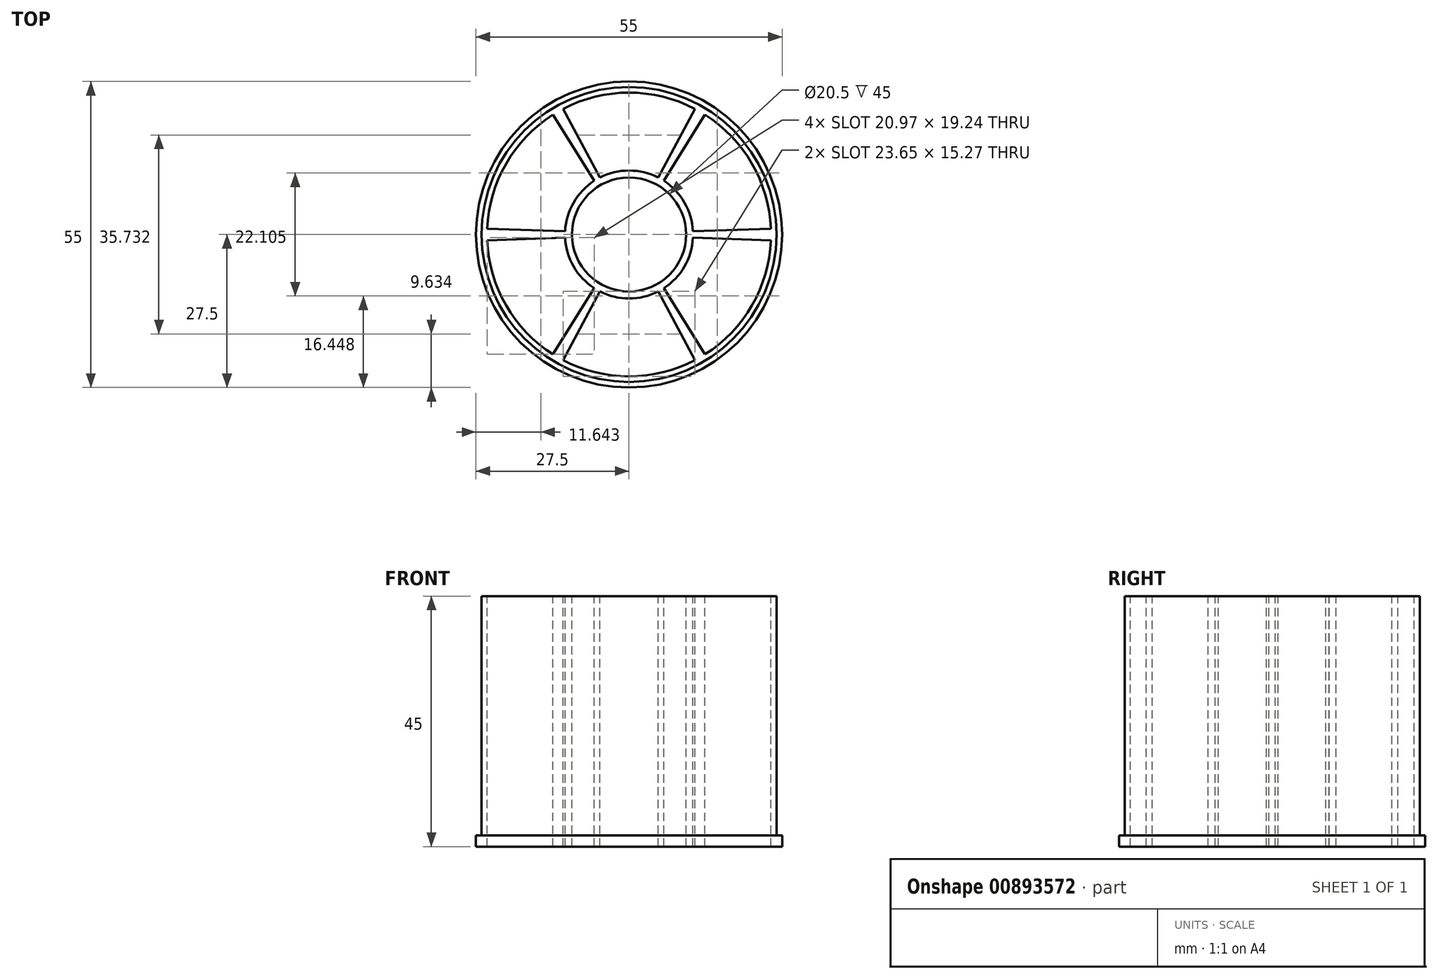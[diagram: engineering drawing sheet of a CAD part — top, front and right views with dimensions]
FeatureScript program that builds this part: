
annotation { "Feature Type Name" : "Feature", "Feature Type Description" : "" }
export const myFeature = defineFeature(function(context is Context, id is Id, definition is map)
    precondition{}
    {
        {
            var Q0;
            Q0=qCreatedBy(makeId("Top.planeOp"),FACE);
            var sketch = newSketch(context, id + "F0", { "sketchPlane" : qUnion([Q0])});
            skCircle(sketch, "E0", {"center": v(0, 0) * mm, "radius": 27.5 * mm});
            skSolve(sketch);
        }
        {
            var Q0;
            Q0 = qSketchRegion(id + "F0", true);
            extrude(context, id + "F1", {"entities" : qUnion([Q0]), "depth" : 45 * mm, "offsetDistance" : 25 * mm});
        }
        {
            var Q0;
            Q0=makeQuery(id+"F1.opExtrude","CAP_FACE",FACE,{"disambiguationData":[OSD([sQuery(id+"F0.wireOp",EDGE,"E0")])],"isStart":false});
            var sketch = newSketch(context, id + "F2", { "sketchPlane" : qUnion([Q0])});
            skCircle(sketch, "E1", {"center": v(0, 0) * mm, "radius": 26.5 * mm});
            skCircle(sketch, "E2", {"center": v(0, 0) * mm, "radius": 41.57 * mm});
            skSolve(sketch);
        }
        {
            var Q0;
            Q0 = qSketchRegion(id + "F2", true);
            extrude(context, id + "F3", {"entities" : qUnion([Q0]), "operationType" : NewBodyOperationType.REMOVE, "oppositeDirection" : true, "depth" : 43 * mm, "offsetDistance" : 25 * mm});
        }
        {
            var Q0;
            Q0=makeQuery(id+"F1.opExtrude","CAP_FACE",FACE,{"disambiguationData":[OSD([sQuery(id+"F0.wireOp",EDGE,"E0")])],"isStart":false});
            var sketch = newSketch(context, id + "F4", { "sketchPlane" : qUnion([Q0])});
            skCircle(sketch, "E3", {"center": v(0, 0) * mm, "radius": 10.25 * mm});
            skSolve(sketch);
        }
        {
            var Q0;
            Q0 = qSketchRegion(id + "F4", true);
            extrude(context, id + "F5", {"entities" : qUnion([Q0]), "operationType" : NewBodyOperationType.REMOVE, "endBound" : BoundingType.THROUGH_ALL, "oppositeDirection" : true, "depth" : 25 * mm, "offsetDistance" : 25 * mm});
        }
        {
            var Q0;
            Q0=makeQuery(id+"F1.opExtrude","CAP_FACE",FACE,{"disambiguationData":[OSD([sQuery(id+"F0.wireOp",EDGE,"E0")])],"isStart":false});
            var sketch = newSketch(context, id + "F6", { "sketchPlane" : qUnion([Q0])});
            skArc(sketch, "E4", {"start": v(5.25, 10.23) * mm, "mid": v(0, 11.5) * mm, "end": v(-5.25, 10.23) * mm});
            skArc(sketch, "E5", {"start": v(11.82, 22.6) * mm, "mid": v(0, 25.5) * mm, "end": v(-11.82, 22.6) * mm});
            skLineSegment(sketch, "E6", {"start": v(-5.25, 10.23) * mm, "end": v(-11.82, 22.6) * mm});
            skLineSegment(sketch, "E7", {"start": v(5.25, 10.23) * mm, "end": v(11.82, 22.6) * mm});
            skLineSegment(sketch, "E8.1.0", {"start": v(-6.24, 9.66) * mm, "end": v(-13.66, 21.54) * mm});
            skArc(sketch, "E8.1.1", {"start": v(-13.66, 21.54) * mm, "mid": v(-22.08, 12.75) * mm, "end": v(-25.48, 1.06) * mm});
            skLineSegment(sketch, "E8.1.2", {"start": v(-11.49, 0.57) * mm, "end": v(-25.48, 1.06) * mm});
            skArc(sketch, "E8.1.3", {"start": v(-6.24, 9.66) * mm, "mid": v(-9.96, 5.75) * mm, "end": v(-11.49, 0.57) * mm});
            skLineSegment(sketch, "E8.2.0", {"start": v(-11.49, -0.57) * mm, "end": v(-25.48, -1.06) * mm});
            skArc(sketch, "E8.2.1", {"start": v(-25.48, -1.06) * mm, "mid": v(-22.08, -12.75) * mm, "end": v(-13.66, -21.54) * mm});
            skLineSegment(sketch, "E8.2.2", {"start": v(-6.24, -9.66) * mm, "end": v(-13.66, -21.54) * mm});
            skArc(sketch, "E8.2.3", {"start": v(-11.49, -0.57) * mm, "mid": v(-9.96, -5.75) * mm, "end": v(-6.24, -9.66) * mm});
            skLineSegment(sketch, "E8.3.0", {"start": v(-5.25, -10.23) * mm, "end": v(-11.82, -22.6) * mm});
            skArc(sketch, "E8.3.1", {"start": v(-11.82, -22.6) * mm, "mid": v(0, -25.5) * mm, "end": v(11.82, -22.6) * mm});
            skLineSegment(sketch, "E8.3.2", {"start": v(5.25, -10.23) * mm, "end": v(11.82, -22.6) * mm});
            skArc(sketch, "E8.3.3", {"start": v(-5.25, -10.23) * mm, "mid": v(0, -11.5) * mm, "end": v(5.25, -10.23) * mm});
            skLineSegment(sketch, "E8.4.0", {"start": v(6.24, -9.66) * mm, "end": v(13.66, -21.54) * mm});
            skArc(sketch, "E8.4.1", {"start": v(13.66, -21.54) * mm, "mid": v(22.08, -12.75) * mm, "end": v(25.48, -1.06) * mm});
            skLineSegment(sketch, "E8.4.2", {"start": v(11.49, -0.57) * mm, "end": v(25.48, -1.06) * mm});
            skArc(sketch, "E8.4.3", {"start": v(6.24, -9.66) * mm, "mid": v(9.96, -5.75) * mm, "end": v(11.49, -0.57) * mm});
            skLineSegment(sketch, "E8.5.0", {"start": v(11.49, 0.57) * mm, "end": v(25.48, 1.06) * mm});
            skArc(sketch, "E8.5.1", {"start": v(25.48, 1.06) * mm, "mid": v(22.08, 12.75) * mm, "end": v(13.66, 21.54) * mm});
            skLineSegment(sketch, "E8.5.2", {"start": v(6.24, 9.66) * mm, "end": v(13.66, 21.54) * mm});
            skArc(sketch, "E8.5.3", {"start": v(11.49, 0.57) * mm, "mid": v(9.96, 5.75) * mm, "end": v(6.24, 9.66) * mm});
            skSolve(sketch);
        }
        {
            var Q0;
            Q0 = qSketchRegion(id + "F6", true);
            extrude(context, id + "F7", {"entities" : qUnion([Q0]), "operationType" : NewBodyOperationType.REMOVE, "endBound" : BoundingType.THROUGH_ALL, "oppositeDirection" : true, "depth" : 25 * mm, "offsetDistance" : 25 * mm});
        }
    });
